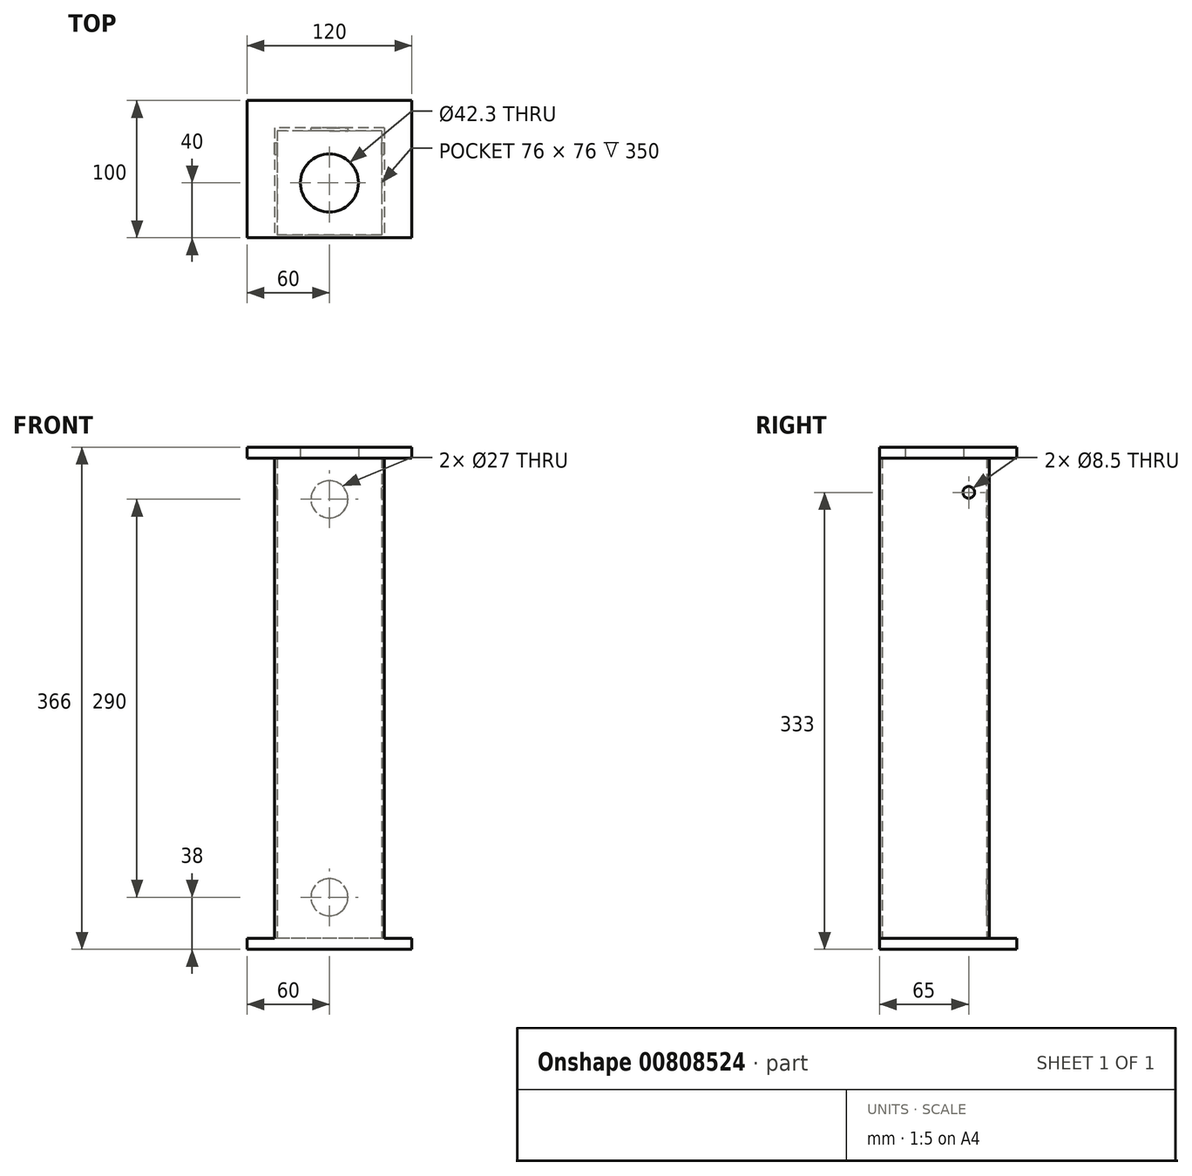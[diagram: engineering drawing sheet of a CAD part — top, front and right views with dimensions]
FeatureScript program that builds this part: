
annotation { "Feature Type Name" : "Feature", "Feature Type Description" : "" }
export const myFeature = defineFeature(function(context is Context, id is Id, definition is map)
    precondition{}
    {
        {
            var Q0;
            Q0=qCreatedBy(makeId("Top.planeOp"),FACE);
            var sketch = newSketch(context, id + "F0", { "sketchPlane" : qUnion([Q0])});
            skLineSegment(sketch, "E0.rect.bottom", {"start": v(60, 60) * mm, "end": v(-60, 60) * mm});
            skLineSegment(sketch, "E0.rect.left", {"start": v(60, 60) * mm, "end": v(60, -40) * mm});
            skLineSegment(sketch, "E0.rect.right", {"start": v(-60, 60) * mm, "end": v(-60, -40) * mm});
            skPoint(sketch, "E0.rect.middle", {"position": v(0, 0) * mm});
            skLineSegment(sketch, "E1.0", {"start": v(60, -40) * mm, "end": v(-60, -40) * mm});
            skSolve(sketch);
        }
        {
            var Q0;
            Q0=qSketchRegion(id+"F0",true);
            extrude(context, id + "F1", {"entities" : qUnion([Q0]), "oppositeDirection" : true, "depth" : 8 * mm});
        }
        {
            var Q0;
            Q0=makeQuery(id+"F0.imprint","IMPRINT",FACE,{"disambiguationData":[TD([[makeQuery(id+"F0.imprint","IMPRINT",EDGE,{"derivedFrom":sQuery(id+"F0.wireOp",EDGE,"E0.rect.bottom")}),1.0]])]});
            var sketch = newSketch(context, id + "F2", { "sketchPlane" : qUnion([Q0])});
            skLineSegment(sketch, "E2.rect.bottom", {"start": v(40, 40) * mm, "end": v(-40, 40) * mm});
            skLineSegment(sketch, "E2.rect.top", {"start": v(40, -40) * mm, "end": v(-40, -40) * mm});
            skLineSegment(sketch, "E2.rect.left", {"start": v(40, 40) * mm, "end": v(40, -40) * mm});
            skLineSegment(sketch, "E2.rect.right", {"start": v(-40, 40) * mm, "end": v(-40, -40) * mm});
            skPoint(sketch, "E2.rect.middle", {"position": v(0, 0) * mm});
            skLineSegment(sketch, "E3.rect.bottom", {"start": v(38, 38) * mm, "end": v(-38, 38) * mm});
            skLineSegment(sketch, "E3.rect.top", {"start": v(38, -38) * mm, "end": v(-38, -38) * mm});
            skLineSegment(sketch, "E3.rect.left", {"start": v(38, 38) * mm, "end": v(38, -38) * mm});
            skLineSegment(sketch, "E3.rect.right", {"start": v(-38, 38) * mm, "end": v(-38, -38) * mm});
            skSolve(sketch);
        }
        {
            var Q0;
            Q0=makeQuery(id+"F2.imprint","IMPRINT",FACE,{"disambiguationData":[TD([[makeQuery(id+"F2.imprint","IMPRINT",EDGE,{"derivedFrom":sQuery(id+"F2.wireOp",EDGE,"E2.rect.bottom")}),1.0]])]});
            extrude(context, id + "F3", {"entities" : qUnion([Q0]), "operationType" : NewBodyOperationType.ADD, "depth" : 350 * mm});
        }
        {
            var Q0;
            Q0=makeQuery(id+"F3.opExtrude","CAP_FACE",FACE,{"disambiguationData":[OSD([sQuery(id+"F2.wireOp",EDGE,"E2.rect.bottom"),sQuery(id+"F2.wireOp",EDGE,"E2.rect.top"),sQuery(id+"F2.wireOp",EDGE,"E2.rect.left"),sQuery(id+"F2.wireOp",EDGE,"E2.rect.right"),sQuery(id+"F2.wireOp",EDGE,"E3.rect.bottom"),sQuery(id+"F2.wireOp",EDGE,"E3.rect.top"),sQuery(id+"F2.wireOp",EDGE,"E3.rect.left"),sQuery(id+"F2.wireOp",EDGE,"E3.rect.right")])],"isStart":false});
            var sketch = newSketch(context, id + "F4", { "sketchPlane" : qUnion([Q0])});
            skLineSegment(sketch, "E4", {"start": v(-40, 40) * mm, "end": v(40, -40) * mm, "construction": true});
            skLineSegment(sketch, "E5.rect.bottom", {"start": v(60, 60) * mm, "end": v(-60, 60) * mm});
            skLineSegment(sketch, "E5.rect.left", {"start": v(60, 60) * mm, "end": v(60, -40) * mm});
            skLineSegment(sketch, "E5.rect.right", {"start": v(-60, 60) * mm, "end": v(-60, -40) * mm});
            skPoint(sketch, "E5.rect.middle", {"position": v(0, 0) * mm});
            skCircle(sketch, "E6", {"center": v(0, 0) * mm, "radius": 21.15 * mm});
            skLineSegment(sketch, "E7.0", {"start": v(60, -40) * mm, "end": v(-60, -40) * mm});
            skSolve(sketch);
        }
        {
            var Q0;
            Q0=qSketchRegion(id+"F4",true);
            extrude(context, id + "F5", {"entities" : qUnion([Q0]), "depth" : 8 * mm});
        }
        {
            var Q0;
            Q0=makeQuery(id+"F3.opExtrude","SWEPT_FACE",FACE,{"disambiguationData":[OSD([sQuery(id+"F2.wireOp",EDGE,"E2.rect.bottom")])]});
            var sketch = newSketch(context, id + "F6", { "sketchPlane" : qUnion([Q0])});
            skPoint(sketch, "E8", {"position": v(0, 320) * mm});
            skCircle(sketch, "E9", {"center": v(0, 320) * mm, "radius": 13.5 * mm});
            skPoint(sketch, "E10", {"position": v(0, 30) * mm});
            skCircle(sketch, "E11", {"center": v(0, 30) * mm, "radius": 13.5 * mm});
            skSolve(sketch);
        }
        {
            var Q0;
            Q0=makeQuery(id+"F6.imprint","IMPRINT",FACE,{"disambiguationData":[TD([[makeQuery(id+"F6.imprint","IMPRINT",EDGE,{"derivedFrom":sQuery(id+"F6.wireOp",EDGE,"E11")}),1.0]])]});
            var Q1;
            Q1=makeQuery(id+"F6.imprint","IMPRINT",FACE,{"disambiguationData":[TD([[makeQuery(id+"F6.imprint","IMPRINT",EDGE,{"derivedFrom":sQuery(id+"F6.wireOp",EDGE,"E9")}),1.0]])]});
            extrude(context, id + "F7", {"entities" : qUnion([Q0, Q1]), "operationType" : NewBodyOperationType.REMOVE, "oppositeDirection" : true, "depth" : 25 * mm});
        }
        {
            var Q0;
            Q0=makeQuery(id+"F3.opExtrude","SWEPT_FACE",FACE,{"disambiguationData":[OSD([sQuery(id+"F2.wireOp",EDGE,"E2.rect.left")])]});
            var sketch = newSketch(context, id + "F8", { "sketchPlane" : qUnion([Q0])});
            skPoint(sketch, "E12", {"position": v(25, 325) * mm});
            skSolve(sketch);
        }
        {
            var Q0;
            Q0=sQuery(id+"F8.wireOp",VERTEX,"E12");
            var Q1;
            Q1=makeQuery(id+"F1.opExtrude","SWEPT_BODY",BODY,{"disambiguationData":[OSD([sQuery(id+"F0.wireOp",EDGE,"E0.rect.bottom"),sQuery(id+"F0.wireOp",EDGE,"E0.rect.left"),sQuery(id+"F0.wireOp",EDGE,"E0.rect.right"),sQuery(id+"F0.wireOp",EDGE,"E1.0")])]});
            hole(context, id + "F9", {"style" : HoleStyle.SIMPLE, "holeDiameter" : 8.5 * mm, "endStyle" : HoleEndStyle.THROUGH, "locations" : qUnion([Q0]), "scope" : qUnion([Q1])});
        }
    });
